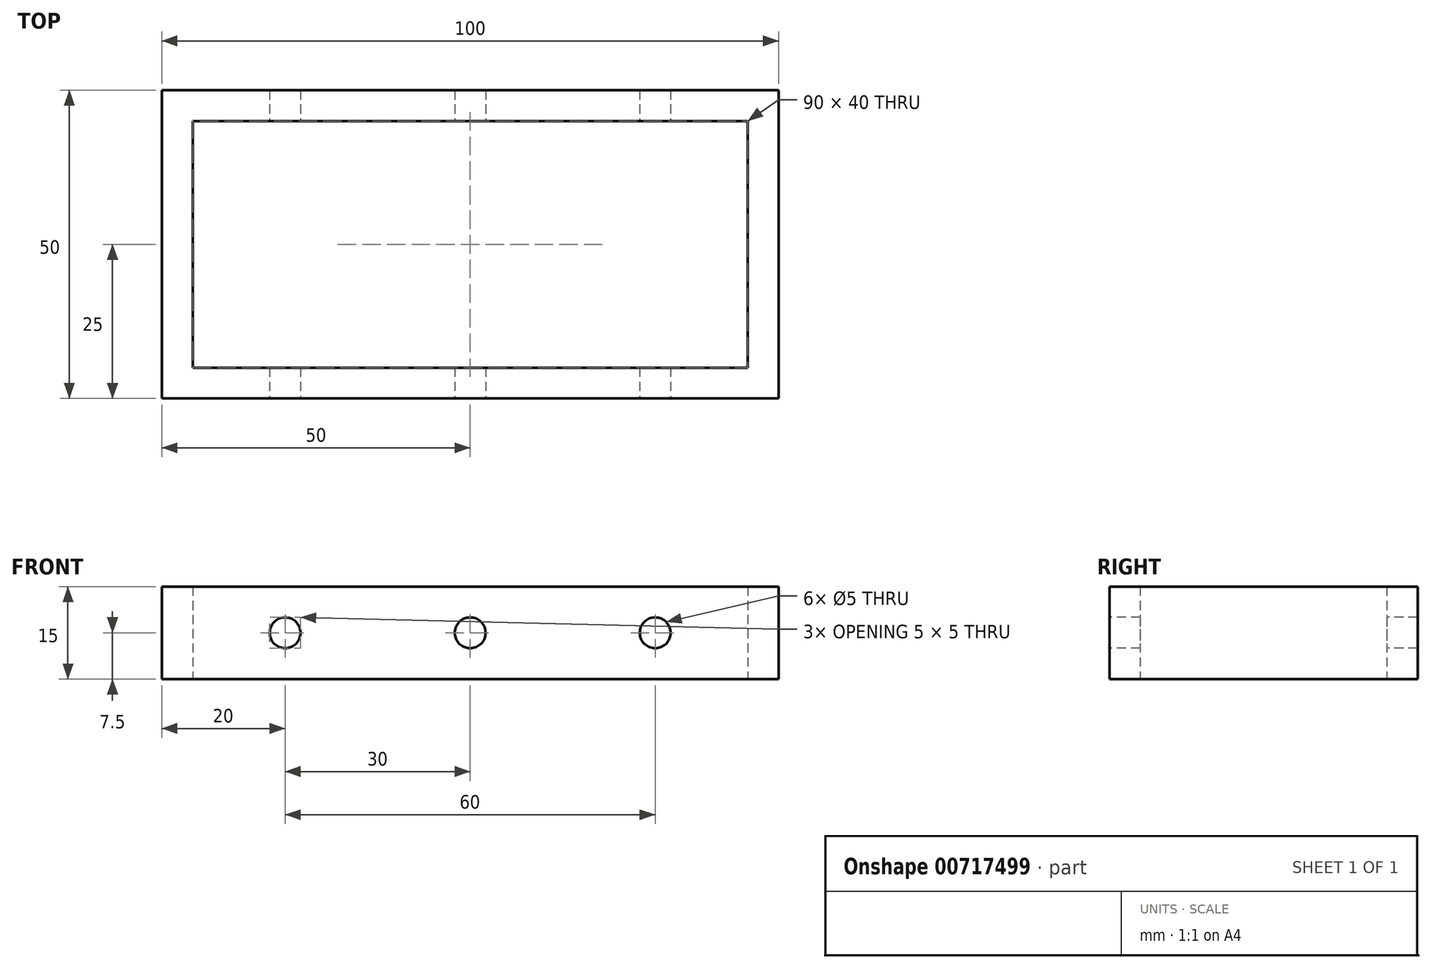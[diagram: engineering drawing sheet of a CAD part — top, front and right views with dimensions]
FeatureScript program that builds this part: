
annotation { "Feature Type Name" : "Feature", "Feature Type Description" : "" }
export const myFeature = defineFeature(function(context is Context, id is Id, definition is map)
    precondition{}
    {
        {
            var Q0;
            Q0=qCreatedBy(makeId("Top.planeOp"),FACE);
            var sketch = newSketch(context, id + "F0", { "sketchPlane" : qUnion([Q0])});
            skLineSegment(sketch, "E0.bottom", {"start": v(-50, 25) * mm, "end": v(50, 25) * mm});
            skLineSegment(sketch, "E0.top", {"start": v(-50, -25) * mm, "end": v(50, -25) * mm});
            skLineSegment(sketch, "E0.left", {"start": v(-50, 25) * mm, "end": v(-50, -25) * mm});
            skLineSegment(sketch, "E0.right", {"start": v(50, 25) * mm, "end": v(50, -25) * mm});
            skPoint(sketch, "E0.middle", {"position": v(0, 0) * mm});
            skLineSegment(sketch, "E1.bottom", {"start": v(-45, 20) * mm, "end": v(45, 20) * mm});
            skLineSegment(sketch, "E1.top", {"start": v(-45, -20) * mm, "end": v(45, -20) * mm});
            skLineSegment(sketch, "E1.left", {"start": v(-45, 20) * mm, "end": v(-45, -20) * mm});
            skLineSegment(sketch, "E1.right", {"start": v(45, 20) * mm, "end": v(45, -20) * mm});
            skSolve(sketch);
        }
        {
            var Q0;
            Q0 = qSketchRegion(id + "F0", true);
            extrude(context, id + "F1", {"entities" : qUnion([Q0]), "depth" : 15 * mm, "offsetDistance" : 25 * mm, "symmetric" : true});
        }
        {
            var Q0;
            Q0=qCreatedBy(makeId("Front.planeOp"),FACE);
            var sketch = newSketch(context, id + "F2", { "sketchPlane" : qUnion([Q0])});
            skCircle(sketch, "E2", {"center": v(0, 0) * mm, "radius": 2.5 * mm});
            skCircle(sketch, "E3", {"center": v(-30, 0) * mm, "radius": 2.5 * mm});
            skCircle(sketch, "E4", {"center": v(30, 0) * mm, "radius": 2.5 * mm});
            skLineSegment(sketch, "E5", {"start": v(0, 7.5) * mm, "end": v(0, -7.5) * mm, "construction": true});
            skSolve(sketch);
        }
        {
            var Q0;
            Q0 = qSketchRegion(id + "F2", true);
            extrude(context, id + "F3", {"entities" : qUnion([Q0]), "operationType" : NewBodyOperationType.REMOVE, "oppositeDirection" : true, "depth" : 50 * mm, "offsetDistance" : 25 * mm, "symmetric" : true});
        }
    });
